# Revit family: Magnuson-YouMe-Desk_Caddy-
name_source: partatom
category: Furniture
units: mm (PartAtom-declared; Revit-internal decimal feet)

## family parameters
Always vertical = Yes
Cut with Voids When Loaded = No
OmniClass Number = 23.40.20.00
OmniClass Title = General Furniture and Specialties
Room Calculation Point = No
Shared = No
Work Plane-Based = No

## types (1)
- YM20-CH
    Assembly Code = E2020200
    Back Finish = MG – Recycled PET
    Body Finish = MG – Recycled PET
    Default Elevation = 0"
    Depth = 7 9/32"
    Description = Personal caddy for laptops, tablets and other items made of Recycled PET with an Oak handle
    Divider Finish = MG – Recycled PET
    Front Finish = MG – Recycled PET
    Height = 11 13/16"
    Keynote = 12500
    Low Emitting Finish = Yes
    Low Emitting Material = Yes
    Manufacturer = Magnuson Group
    Model = YM20-CH
    Percentage of Recycled Content = 0
    Rail Finish = MG - Wood
    Revit File Built By = https://servex-us.com
    Salvage or Reuse = Yes
    Strap Finish = MG - Elastic (Strap)
    Type Comments = YouMe
    URL = www.magnusongroup.com
    Width = 13 31/32"

## geometry (parser evidence)
native form markers: Sweep x1
no freeform markers — native parametric forms only
